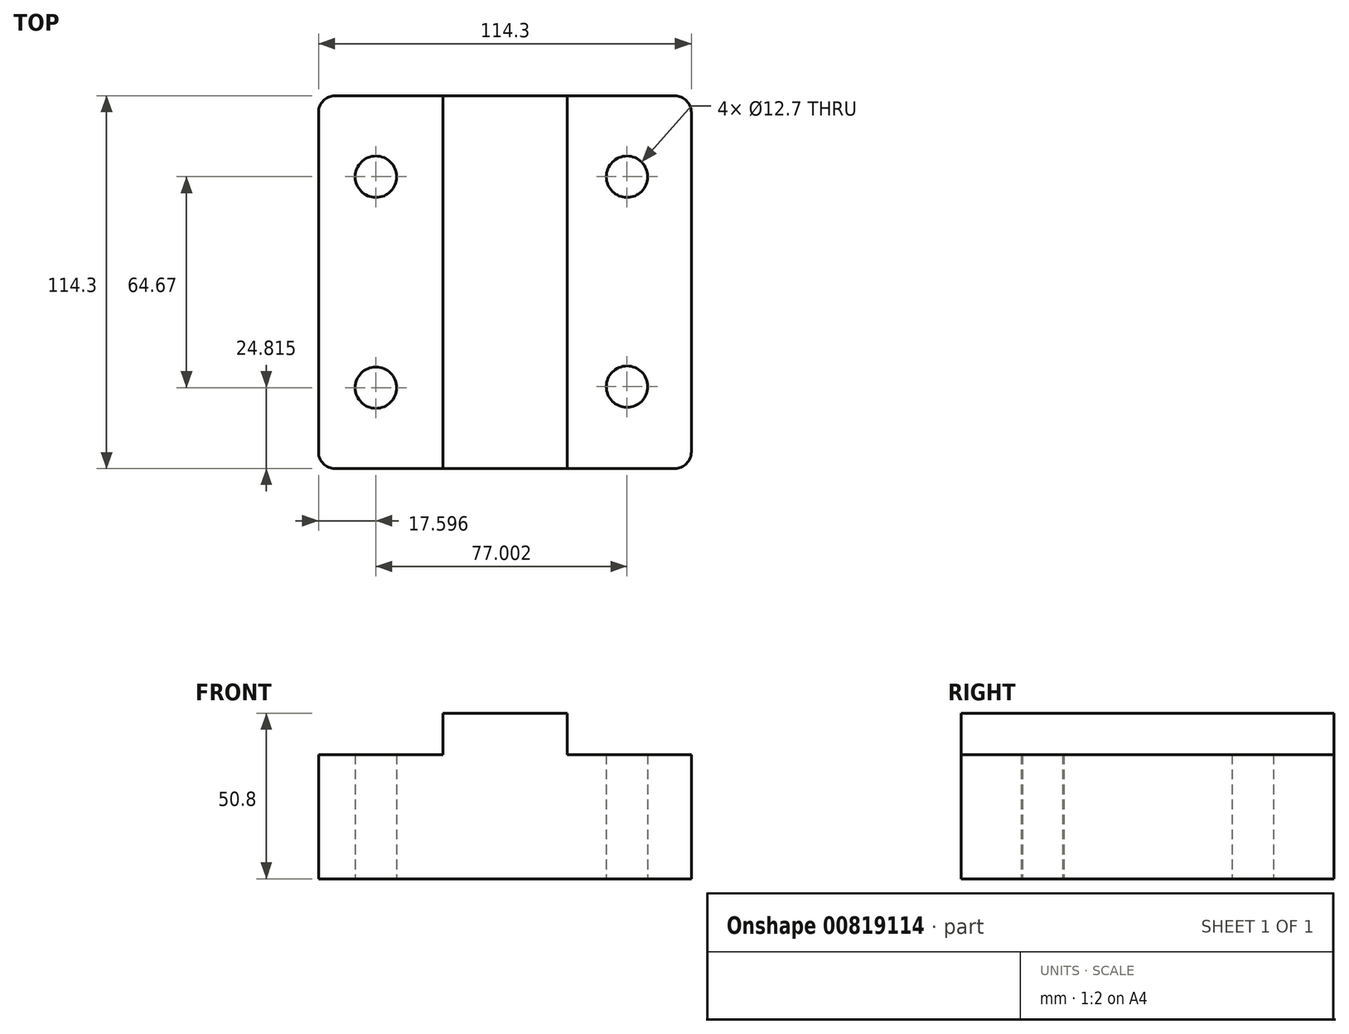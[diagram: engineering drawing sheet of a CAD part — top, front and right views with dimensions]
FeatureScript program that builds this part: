
annotation { "Feature Type Name" : "Feature", "Feature Type Description" : "" }
export const myFeature = defineFeature(function(context is Context, id is Id, definition is map)
    precondition{}
    {
        {
            var Q0;
            Q0=qCreatedBy(makeId("Top.planeOp"),FACE);
            var sketch = newSketch(context, id + "F0", { "sketchPlane" : qUnion([Q0])});
            skLineSegment(sketch, "E0.bottom", {"start": v(-19.05, 57.15) * mm, "end": v(19.05, 57.15) * mm});
            skLineSegment(sketch, "E0.top", {"start": v(-19.05, -57.15) * mm, "end": v(19.05, -57.15) * mm});
            skLineSegment(sketch, "E0.left", {"start": v(-19.05, 57.15) * mm, "end": v(-19.05, -57.15) * mm});
            skLineSegment(sketch, "E0.right", {"start": v(19.05, 57.15) * mm, "end": v(19.05, -57.15) * mm});
            skPoint(sketch, "E0.middle", {"position": v(0, 0) * mm});
            skSolve(sketch);
        }
        {
            var Q0;
            Q0=qCreatedBy(makeId("Top.planeOp"),FACE);
            var sketch = newSketch(context, id + "F1", { "sketchPlane" : qUnion([Q0])});
            skLineSegment(sketch, "E1.bottom", {"start": v(-19.05, 57.15) * mm, "end": v(-57.15, 57.15) * mm});
            skLineSegment(sketch, "E1.top", {"start": v(-19.05, -57.15) * mm, "end": v(-57.15, -57.15) * mm});
            skLineSegment(sketch, "E1.left", {"start": v(-19.05, 57.15) * mm, "end": v(-19.05, -57.15) * mm});
            skLineSegment(sketch, "E1.right", {"start": v(-57.15, 57.15) * mm, "end": v(-57.15, -57.15) * mm});
            skPoint(sketch, "E2", {"position": v(-39.55, 32.33) * mm});
            skPoint(sketch, "E3", {"position": v(-39.55, -32.33) * mm});
            skSolve(sketch);
        }
        {
            var Q0;
            Q0=qCreatedBy(makeId("Top.planeOp"),FACE);
            var sketch = newSketch(context, id + "F2", { "sketchPlane" : qUnion([Q0])});
            skLineSegment(sketch, "E4.bottom", {"start": v(19.05, 57.15) * mm, "end": v(57.15, 57.15) * mm});
            skLineSegment(sketch, "E4.top", {"start": v(19.05, -57.15) * mm, "end": v(57.15, -57.15) * mm});
            skLineSegment(sketch, "E4.left", {"start": v(19.05, 57.15) * mm, "end": v(19.05, -57.15) * mm});
            skLineSegment(sketch, "E4.right", {"start": v(57.15, 57.15) * mm, "end": v(57.15, -57.15) * mm});
            skPoint(sketch, "E5", {"position": v(37.45, 32.33) * mm});
            skPoint(sketch, "E6", {"position": v(37.45, -32.03) * mm});
            skSolve(sketch);
        }
        {
            var Q0;
            Q0 = qSketchRegion(id + "F0", true);
            extrude(context, id + "F3", {"entities" : qUnion([Q0]), "depth" : 50.8 * mm, "offsetDistance" : 25.4 * mm});
        }
        {
            var Q0;
            Q0 = qSketchRegion(id + "F2", true);
            extrude(context, id + "F4", {"entities" : qUnion([Q0]), "operationType" : NewBodyOperationType.ADD, "depth" : 38.1 * mm, "offsetDistance" : 25.4 * mm});
        }
        {
            var Q0;
            Q0 = qSketchRegion(id + "F1", true);
            extrude(context, id + "F5", {"entities" : qUnion([Q0]), "operationType" : NewBodyOperationType.ADD, "depth" : 38.1 * mm, "offsetDistance" : 25.4 * mm});
        }
        {
            var Q0;
            Q0=sQuery(id+"F2.wireOp",VERTEX,"E5");
            var Q1;
            Q1=makeQuery(id+"F3.opExtrude","SWEPT_BODY",BODY,{"disambiguationData":[OSD([sQuery(id+"F0.wireOp",EDGE,"E0.bottom"),sQuery(id+"F0.wireOp",EDGE,"E0.top"),sQuery(id+"F0.wireOp",EDGE,"E0.left"),sQuery(id+"F0.wireOp",EDGE,"E0.right")])]});
            hole(context, id + "F6", {"style" : HoleStyle.SIMPLE, "endStyle" : HoleEndStyle.THROUGH, "oppositeDirection" : true, "holeDiameter" : 12.7 * mm, "majorDiameter" : 6.35 * mm, "isTappedThrough" : true, "tappedDepth" : 12.7 * mm, "tapClearance" : 3, "locations" : qUnion([Q0]), "scope" : qUnion([Q1])});
        }
        {
            var Q0;
            Q0=sQuery(id+"F2.wireOp",VERTEX,"E6");
            var Q1;
            Q1=makeQuery(id+"F3.opExtrude","SWEPT_BODY",BODY,{"disambiguationData":[OSD([sQuery(id+"F0.wireOp",EDGE,"E0.bottom"),sQuery(id+"F0.wireOp",EDGE,"E0.top"),sQuery(id+"F0.wireOp",EDGE,"E0.left"),sQuery(id+"F0.wireOp",EDGE,"E0.right")])]});
            hole(context, id + "F7", {"style" : HoleStyle.SIMPLE, "endStyle" : HoleEndStyle.THROUGH, "oppositeDirection" : true, "holeDiameter" : 12.7 * mm, "majorDiameter" : 6.35 * mm, "isTappedThrough" : true, "tappedDepth" : 12.7 * mm, "tapClearance" : 3, "locations" : qUnion([Q0]), "scope" : qUnion([Q1])});
        }
        {
            var Q0;
            Q0=sQuery(id+"F1.wireOp",VERTEX,"E2");
            var Q1;
            Q1=makeQuery(id+"F3.opExtrude","SWEPT_BODY",BODY,{"disambiguationData":[OSD([sQuery(id+"F0.wireOp",EDGE,"E0.bottom"),sQuery(id+"F0.wireOp",EDGE,"E0.top"),sQuery(id+"F0.wireOp",EDGE,"E0.left"),sQuery(id+"F0.wireOp",EDGE,"E0.right")])]});
            hole(context, id + "F8", {"style" : HoleStyle.SIMPLE, "endStyle" : HoleEndStyle.THROUGH, "oppositeDirection" : true, "holeDiameter" : 12.7 * mm, "majorDiameter" : 6.35 * mm, "isTappedThrough" : true, "tappedDepth" : 12.7 * mm, "tapClearance" : 3, "locations" : qUnion([Q0]), "scope" : qUnion([Q1])});
        }
        {
            var Q0;
            Q0=sQuery(id+"F1.wireOp",VERTEX,"E3");
            var Q1;
            Q1=makeQuery(id+"F3.opExtrude","SWEPT_BODY",BODY,{"disambiguationData":[OSD([sQuery(id+"F0.wireOp",EDGE,"E0.bottom"),sQuery(id+"F0.wireOp",EDGE,"E0.top"),sQuery(id+"F0.wireOp",EDGE,"E0.left"),sQuery(id+"F0.wireOp",EDGE,"E0.right")])]});
            hole(context, id + "F9", {"style" : HoleStyle.SIMPLE, "endStyle" : HoleEndStyle.THROUGH, "oppositeDirection" : true, "holeDiameter" : 12.7 * mm, "majorDiameter" : 6.35 * mm, "isTappedThrough" : true, "tappedDepth" : 12.7 * mm, "tapClearance" : 3, "locations" : qUnion([Q0]), "scope" : qUnion([Q1])});
        }
        {
            var Q0;
            Q0=makeQuery(id+"F5.opExtrude","SWEPT_EDGE",EDGE,{"disambiguationData":[OSD([sQuery(id+"F1.wireOp",EDGE,"E1.top"),sQuery(id+"F1.wireOp",EDGE,"E1.right")])]});
            fillet(context, id + "F10", {"entities" : qUnion([Q0]), "radius" : 5.08 * mm, "tangentPropagation" : true, "allowEdgeOverflow" : false});
        }
        {
            var Q0;
            Q0=makeQuery(id+"F4.opExtrude","SWEPT_EDGE",EDGE,{"disambiguationData":[OSD([sQuery(id+"F2.wireOp",EDGE,"E4.top"),sQuery(id+"F2.wireOp",EDGE,"E4.right")])]});
            fillet(context, id + "F11", {"entities" : qUnion([Q0]), "radius" : 5.08 * mm, "tangentPropagation" : true, "allowEdgeOverflow" : false});
        }
        {
            var Q0;
            Q0=makeQuery(id+"F4.opExtrude","SWEPT_EDGE",EDGE,{"disambiguationData":[OSD([sQuery(id+"F2.wireOp",EDGE,"E4.bottom"),sQuery(id+"F2.wireOp",EDGE,"E4.right")])]});
            fillet(context, id + "F12", {"entities" : qUnion([Q0]), "radius" : 5.08 * mm, "tangentPropagation" : true, "allowEdgeOverflow" : false});
        }
        {
            var Q0;
            Q0=makeQuery(id+"F5.opExtrude","SWEPT_EDGE",EDGE,{"disambiguationData":[OSD([sQuery(id+"F1.wireOp",EDGE,"E1.bottom"),sQuery(id+"F1.wireOp",EDGE,"E1.right")])]});
            fillet(context, id + "F13", {"entities" : qUnion([Q0]), "radius" : 5.08 * mm, "tangentPropagation" : true, "allowEdgeOverflow" : false});
        }
    });
